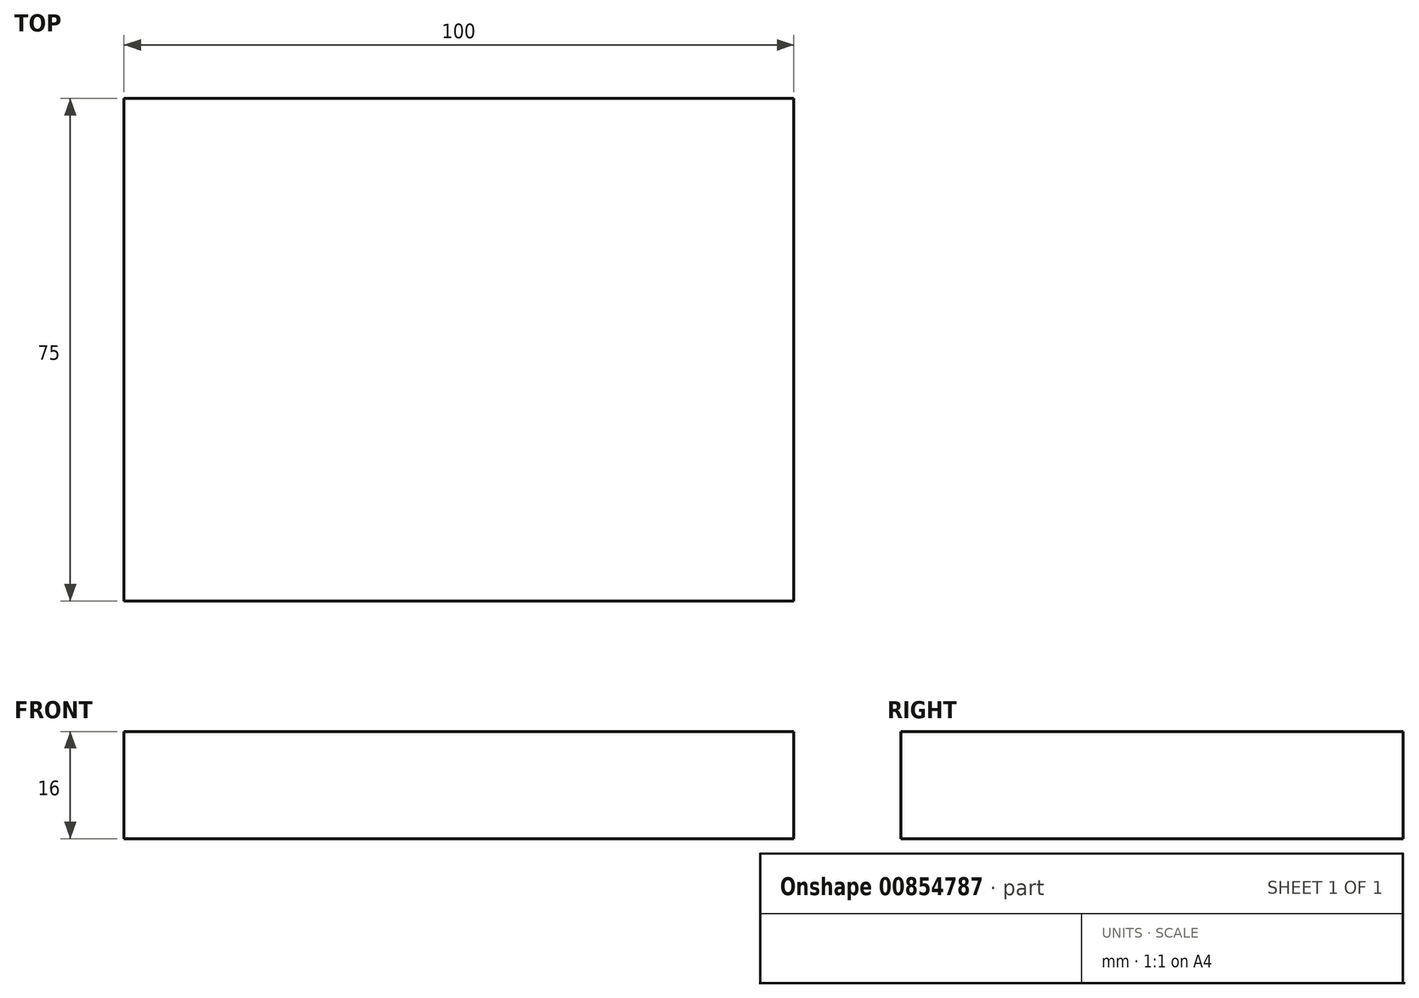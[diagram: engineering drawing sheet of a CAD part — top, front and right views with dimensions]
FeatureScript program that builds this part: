
annotation { "Feature Type Name" : "Feature", "Feature Type Description" : "" }
export const myFeature = defineFeature(function(context is Context, id is Id, definition is map)
    precondition{}
    {
        {
            var Q0;
            Q0=qCreatedBy(makeId("Top.planeOp"),FACE);
            var sketch = newSketch(context, id + "F0", { "sketchPlane" : qUnion([Q0])});
            skLineSegment(sketch, "E0.bottom", {"start": v(0, 0) * mm, "end": v(100, 0) * mm});
            skLineSegment(sketch, "E0.top", {"start": v(0, 75) * mm, "end": v(100, 75) * mm});
            skLineSegment(sketch, "E0.left", {"start": v(0, 0) * mm, "end": v(0, 75) * mm});
            skLineSegment(sketch, "E0.right", {"start": v(100, 0) * mm, "end": v(100, 75) * mm});
            skSolve(sketch);
        }
        {
            var Q0;
            Q0 = qSketchRegion(id + "F0", true);
            extrude(context, id + "F1", {"entities" : qUnion([Q0]), "depth" : 16 * mm, "offsetDistance" : 25 * mm});
        }
    });
